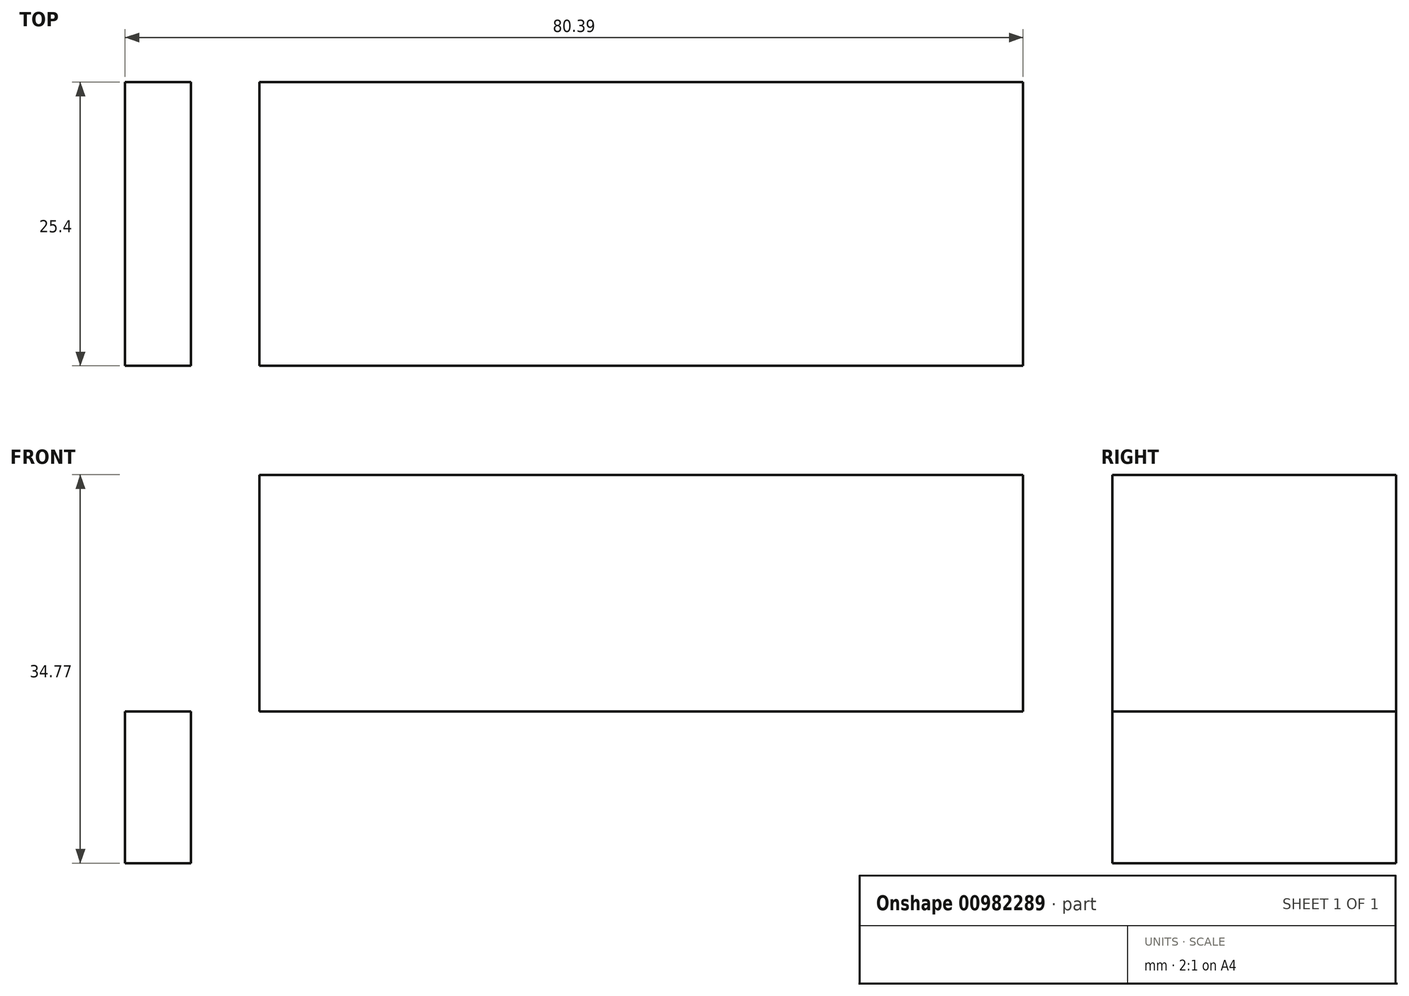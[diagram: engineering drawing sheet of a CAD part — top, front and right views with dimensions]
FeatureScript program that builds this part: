
annotation { "Feature Type Name" : "Feature", "Feature Type Description" : "" }
export const myFeature = defineFeature(function(context is Context, id is Id, definition is map)
    precondition{}
    {
        {
            var Q0;
            Q0=qCreatedBy(makeId("Front.planeOp"),FACE);
            var sketch = newSketch(context, id + "F0", { "sketchPlane" : qUnion([Q0])});
            skLineSegment(sketch, "E0.bottom", {"start": v(-6.14, 0) * mm, "end": v(-12.02, 0) * mm});
            skLineSegment(sketch, "E0.top", {"start": v(-6.14, -13.6) * mm, "end": v(-12.02, -13.6) * mm});
            skLineSegment(sketch, "E0.left", {"start": v(-6.14, 0) * mm, "end": v(-6.14, -13.6) * mm});
            skLineSegment(sketch, "E0.right", {"start": v(-12.02, 0) * mm, "end": v(-12.02, -13.6) * mm});
            skLineSegment(sketch, "E1.bottom", {"start": v(0, 0) * mm, "end": v(68.37, 0) * mm});
            skLineSegment(sketch, "E1.top", {"start": v(0, 21.18) * mm, "end": v(68.37, 21.18) * mm});
            skLineSegment(sketch, "E1.left", {"start": v(0, 0) * mm, "end": v(0, 21.18) * mm});
            skLineSegment(sketch, "E1.right", {"start": v(68.37, 0) * mm, "end": v(68.37, 21.18) * mm});
            skSolve(sketch);
        }
        {
            var Q0;
            Q0 = qSketchRegion(id + "F0", true);
            extrude(context, id + "F1", {"entities" : qUnion([Q0]), "depth" : 25.4 * mm, "offsetDistance" : 25.4 * mm});
        }
    });
